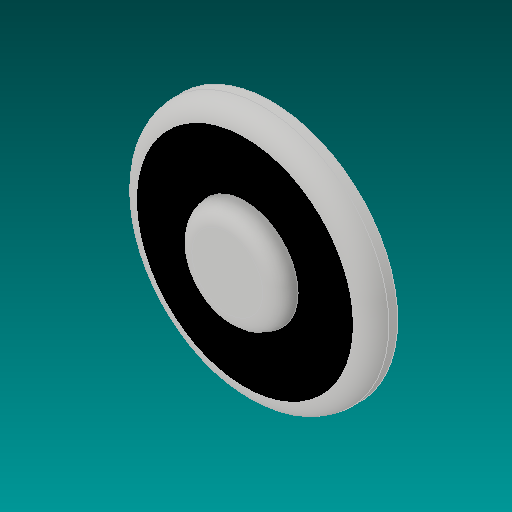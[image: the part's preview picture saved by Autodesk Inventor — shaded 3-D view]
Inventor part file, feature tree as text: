
AUTODESK INVENTOR PART (.ipt)
format: ipt  version: 2020 (Build 240168000, 168)  size: 159,232 bytes
history: native  units: mm
features: extrude x4, sketch x4, fillet x3
ambient origin geometry x8: Origin, YZ Plane, XZ Plane, XY Plane, X Axis, Y Axis, Z Axis, Center Point
bodies: Solid1 (feature_tree)
feature tree (11):
  extrude  "Extrusion1"  Depth=3.0mm TaperAngle=0.0deg
  extrude  "Extrusion2"  Depth=2.0mm TaperAngle=0.0deg
  fillet  "Fillet1"  Radius=2.0mm
  fillet  "Fillet2"  Radius=2.0mm
  extrude  "Extrusion3"  Depth=2.0mm TaperAngle=0.0deg
  extrude  "Extrusion4"  [1 undecoded]
  fillet  "Fillet3"  [1 undecoded]
  sketch  "Sketch1"  dims[d0=28.5mm d1=3.0mm d2=0.0mm]
  sketch  "Sketch2"  dims[d3=12.0mm d4=2.0mm d5=0.0mm d6=2.0mm d7=2.0mm]
  sketch  "Sketch3"  dims[d8=0.5mm d9=0.0mm d10=2.0mm d11=0.0mm]
  sketch  "Sketch4"  dims[d12=2.0mm]
note: 2 required parameter values undecoded (feature->parameter linkage not recoverable at this tier; creation-order binding heuristic only, values carry confidence <= 0.55)
